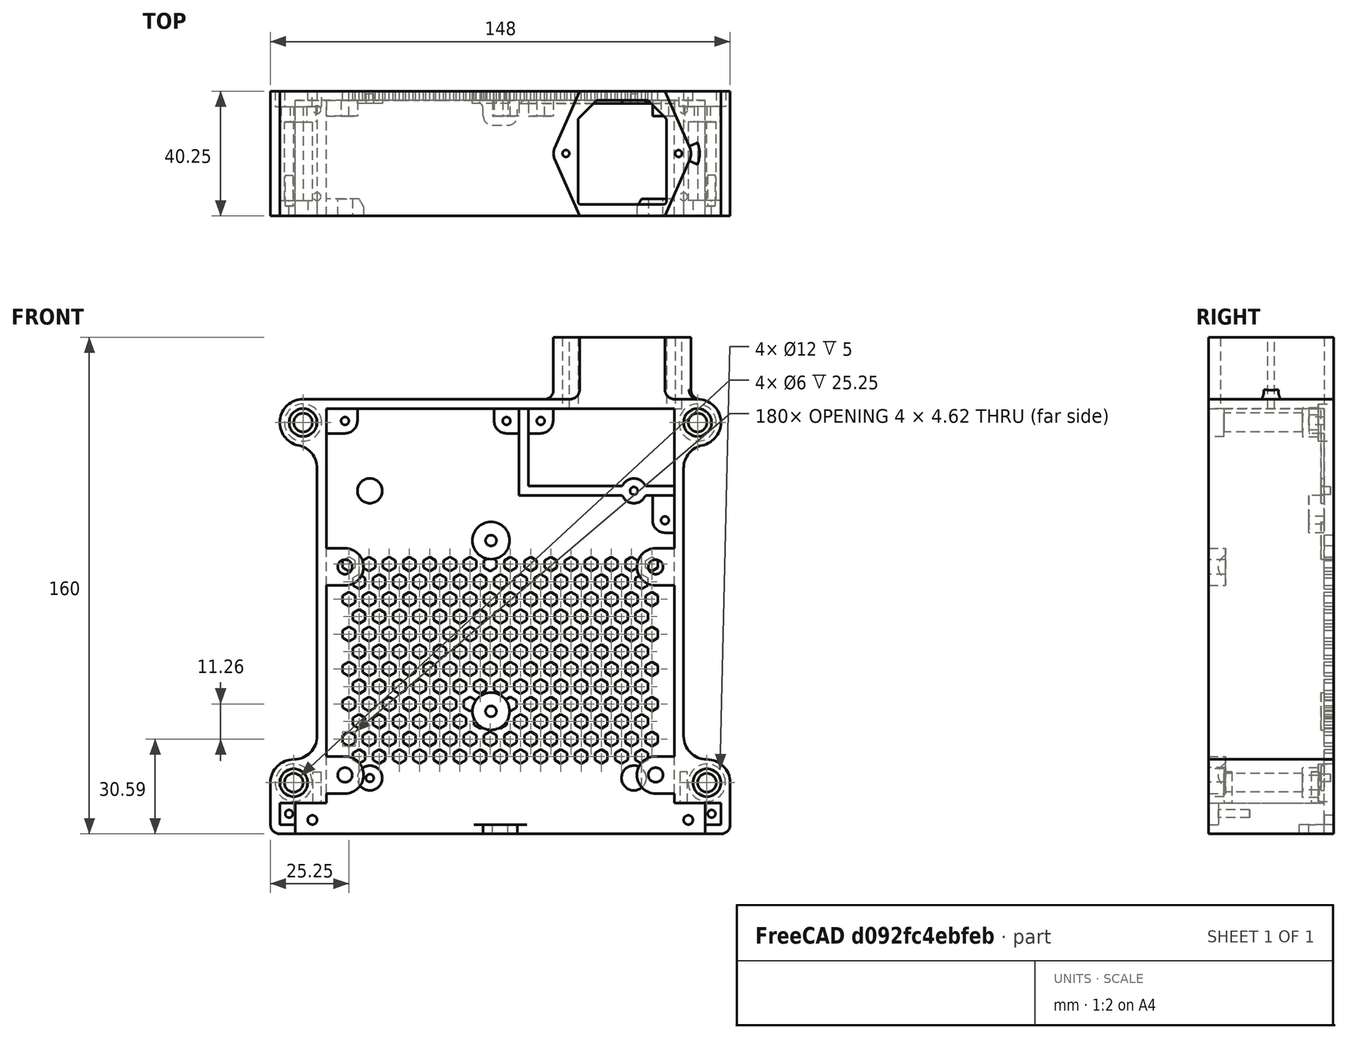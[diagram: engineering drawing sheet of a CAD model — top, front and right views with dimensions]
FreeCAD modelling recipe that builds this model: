
FCSTD DOCUMENT  (FreeCAD 1.0R39319 (Git))
Label: Stack_Module_PSU
License: All rights reserved
LicenseURL: https://en.wikipedia.org/wiki/All_rights_reserved
objects: Sketcher::SketchObject×24, PartDesign::Pocket×17, PartDesign::Pad×7, PartDesign::Fillet×6, PartDesign::LinearPattern×3, PartDesign::MultiTransform×1, PartDesign::Mirrored×1, PartDesign::CoordinateSystem×1, PartDesign::Body×1, App::Part×1
note: 150 computed .brp shape members not serialized (recipe doc carries the construction recipe); baked Part::Feature solids carry a one-line shape summary decoded from their .brp

FEATURE [Sketcher::SketchObject] Sketch
  ArcFitTolerance = 1e-06
  AttachmentSupport = -> [XZ_Plane001]
  FullyConstrained = true
  MakeInternals = false
  MapMode = 5
  Placement = pos=(0,0,0) rot=(1,0,0;1.5708rad)
  sketch-geometry (9):
    g0: LineSegment StartX=0 StartY=-70 StartZ=0 EndX=74 EndY=-70 EndZ=0
    g1: LineSegment StartX=74 StartY=-70 StartZ=0 EndX=74 EndY=-53.5 EndZ=0
    g2: ArcOfCircle CenterX=66.5 CenterY=-53.5 CenterZ=0 NormalX=0 NormalY=0 NormalZ=1 AngleXU=0 Radius=7.5 StartAngle=0 EndAngle=1.5708
    g3: ArcOfCircle CenterX=66.5 CenterY=-38.5 CenterZ=0 NormalX=0 NormalY=0 NormalZ=1 AngleXU=0 Radius=7.5 StartAngle=3.14159 EndAngle=4.71239
    g4: LineSegment StartX=59 StartY=-38.5 StartZ=0 EndX=59 EndY=47.8031 EndZ=0
    g5: ArcOfCircle CenterX=66.5 CenterY=47.8031 CenterZ=0 NormalX=0 NormalY=0 NormalZ=1 AngleXU=0 Radius=7.5 StartAngle=1.77215 EndAngle=3.14159
    g6: ArcOfCircle CenterX=63.5 CenterY=62.5 CenterZ=0 NormalX=0 NormalY=0 NormalZ=1 AngleXU=0 Radius=7.5 StartAngle=4.91375 EndAngle=7.85398
    g7: LineSegment StartX=63.5 StartY=70 StartZ=0 EndX=0 EndY=70 EndZ=0
    g8: LineSegment StartX=0 StartY=70 StartZ=0 EndX=0 EndY=-70 EndZ=0
  constraints (26):
    c: PointOnObject(g0,g-2)
    c: Horizontal(g0)
    c: Coincident(g0,g1)
    c: Vertical(g1)
    c: Tangent(g1,g2) = -1.5708
    c: Tangent(g2,g3) = 1.5708
    c: Tangent(g3,g4) = 1.5708
    c: Tangent(g4,g5) = 1.5708
    c: Tangent(g5,g6) = 1.5708
    c: Tangent(g6,g7) = -1.5708
    c: Coincident(g7,g8)
    c: Coincident(g8,g0)
    c: Vertical(g8)
    c: Horizontal(g7)
    c: Vertical(g4)
    c: DistanceX(g0,g0) = 74
    c: Distance(g7,g0) = 140
    c: Distance(g2,g0) = 16.5
    c: Radius(g2) = 7.5
    c: Distance(g8,g4) = 59
    c: Radius(g6) = 7.5
    c: Distance(g6,g8) = 63.5
    c: Distance(g2,g8) = 66.5
    c: Distance(g-1,g0) = 70
    c: Radius(g3) = 7.5
    c: Radius(g5) = 7.5
FEATURE [PartDesign::Pad] Pad
  Direction = (0,-1,2e-16)
  Length = 40.25
  Length2 = 10
  Placement = pos=(0,0,0) rot=(1,0,0;1.5708rad)
  Profile = -> Sketch
  ReferenceAxis = -> Sketch [N_Axis]
  Refine = true
  Suppressed = false
  Type = 0
FEATURE [Sketcher::SketchObject] Sketch001
  ArcFitTolerance = 1e-06
  AttachmentSupport = -> [Pad]
  ExternalGeometry = -> [Pad]
  FullyConstrained = true
  MakeInternals = false
  MapMode = 5
  Placement = pos=(0,-40.25,0) rot=(1,0,0;1.5708rad)
  sketch-geometry (4):
    g0: LineSegment StartX=0 StartY=-70 StartZ=0 EndX=66 EndY=-70 EndZ=0
    g1: LineSegment StartX=66 StartY=-70 StartZ=0 EndX=66 EndY=-60 EndZ=0
    g2: LineSegment StartX=66 StartY=-60 StartZ=0 EndX=0 EndY=-60 EndZ=0
    g3: LineSegment StartX=0 StartY=-60 StartZ=0 EndX=0 EndY=-70 EndZ=0
  constraints (11):
    c: Coincident(g0,g1)
    c: Coincident(g1,g2)
    c: Coincident(g2,g3)
    c: Coincident(g3,g0)
    c: Horizontal(g0)
    c: Horizontal(g2)
    c: Vertical(g1)
    c: Vertical(g3)
    c: Coincident(g0,g-3)
    c: Distance(g0,g2) = 10
    c: Distance(g1,g3) = 66
FEATURE [PartDesign::Pocket] Pocket
  BaseFeature = -> Pad
  Direction = (0,1,-2e-16)
  Length = 0
  Length2 = 5
  Offset = -3
  Placement = pos=(0,0,0) rot=(1,0,0;1.5708rad)
  Profile = -> Sketch001
  ReferenceAxis = -> Sketch001 [N_Axis]
  Refine = true
  Suppressed = false
  Type = 3
  UpToFace = -> Pad [Face10]
FEATURE [Sketcher::SketchObject] Sketch002
  ArcFitTolerance = 1e-06
  AttachmentSupport = -> [Pocket]
  ExternalGeometry = -> [Pocket]
  FullyConstrained = true
  MakeInternals = false
  MapMode = 5
  Placement = pos=(0,-40.25,0) rot=(1,0,0;1.5708rad)
  sketch-geometry (4):
    g0: LineSegment StartX=0 StartY=67 StartZ=0 EndX=0 EndY=-60 EndZ=0
    g1: LineSegment StartX=0 StartY=-60 StartZ=0 EndX=56 EndY=-60 EndZ=0
    g2: LineSegment StartX=56 StartY=-60 StartZ=0 EndX=56 EndY=67 EndZ=0
    g3: LineSegment StartX=56 StartY=67 StartZ=0 EndX=0 EndY=67 EndZ=0
  constraints (12):
    c: Coincident(g0,g1)
    c: Coincident(g1,g2)
    c: Coincident(g2,g3)
    c: Coincident(g3,g0)
    c: Vertical(g0)
    c: Vertical(g2)
    c: Horizontal(g1)
    c: Horizontal(g3)
    c: PointOnObject(g0,g-2)
    c: PointOnObject(g1,g-5)
    c: Distance(g-4,g2) = 3
    c: Distance(g-3,g3) = 3
FEATURE [PartDesign::Pocket] Pocket001
  BaseFeature = -> Pocket
  Direction = (0,1,-2e-16)
  Length = 0
  Length2 = 5
  Placement = pos=(0,0,0) rot=(1,0,0;1.5708rad)
  Profile = -> Sketch002
  ReferenceAxis = -> Sketch002 [N_Axis]
  Refine = true
  Suppressed = false
  Type = 3
  UpToFace = -> Pocket [Face6]
FEATURE [Sketcher::SketchObject] Sketch003
  ArcFitTolerance = 1e-06
  AttachmentSupport = -> [Pocket001]
  FullyConstrained = true
  MakeInternals = false
  MapMode = 5
  Placement = pos=(0,-3,0) rot=(1,0,0;1.5708rad)
  sketch-geometry (28):
    g0: LineSegment StartX=2 StartY=1.1547 StartZ=0 EndX=0 EndY=2.3094 EndZ=0
    g1: LineSegment StartX=0 StartY=2.3094 StartZ=0 EndX=-2 EndY=1.1547 EndZ=0
    g2: LineSegment StartX=-2 StartY=1.1547 StartZ=0 EndX=-2 EndY=-1.1547 EndZ=0
    g3: LineSegment StartX=-2 StartY=-1.1547 StartZ=0 EndX=0 EndY=-2.3094 EndZ=0
    g4: LineSegment StartX=0 StartY=-2.3094 StartZ=0 EndX=2 EndY=-1.1547 EndZ=0
    g5: LineSegment StartX=2 StartY=-1.1547 StartZ=0 EndX=2 EndY=1.1547 EndZ=0
    g6: Circle [constr] CenterX=0 CenterY=0 CenterZ=0 NormalX=0 NormalY=0 NormalZ=1 AngleXU=0 Radius=2.3094
    g7: LineSegment StartX=5.25 StartY=6.7847 StartZ=0 EndX=3.25 EndY=7.9394 EndZ=0
    g8: LineSegment StartX=3.25 StartY=7.9394 StartZ=0 EndX=1.25 EndY=6.7847 EndZ=0
    g9: LineSegment StartX=1.25 StartY=6.7847 StartZ=0 EndX=1.25 EndY=4.4753 EndZ=0
    g10: LineSegment StartX=1.25 StartY=4.4753 StartZ=0 EndX=3.25 EndY=3.3206 EndZ=0
    g11: LineSegment StartX=3.25 StartY=3.3206 StartZ=0 EndX=5.25 EndY=4.4753 EndZ=0
    g12: LineSegment StartX=5.25 StartY=4.4753 StartZ=0 EndX=5.25 EndY=6.7847 EndZ=0
    g13: Circle [constr] CenterX=3.25 CenterY=5.63 CenterZ=0 NormalX=0 NormalY=0 NormalZ=1 AngleXU=0 Radius=2.3094
    g14: LineSegment StartX=6.5 StartY=2.3094 StartZ=0 EndX=4.5 EndY=1.1547 EndZ=0
    g15: LineSegment StartX=4.5 StartY=1.1547 StartZ=0 EndX=4.5 EndY=-1.1547 EndZ=0
    g16: LineSegment StartX=4.5 StartY=-1.1547 StartZ=0 EndX=6.5 EndY=-2.3094 EndZ=0
    g17: LineSegment StartX=6.5 StartY=-2.3094 StartZ=0 EndX=8.5 EndY=-1.1547 EndZ=0
    g18: LineSegment StartX=8.5 StartY=-1.1547 StartZ=0 EndX=8.5 EndY=1.1547 EndZ=0
    g19: LineSegment StartX=8.5 StartY=1.1547 StartZ=0 EndX=6.5 EndY=2.3094 EndZ=0
    g20: Circle [constr] CenterX=6.5 CenterY=0 CenterZ=0 NormalX=0 NormalY=0 NormalZ=1 AngleXU=0 Radius=2.3094
    g21: LineSegment StartX=11.75 StartY=6.7847 StartZ=0 EndX=9.75 EndY=7.9394 EndZ=0
    g22: LineSegment StartX=9.75 StartY=7.9394 StartZ=0 EndX=7.75 EndY=6.7847 EndZ=0
    g23: LineSegment StartX=7.75 StartY=6.7847 StartZ=0 EndX=7.75 EndY=4.4753 EndZ=0
    g24: LineSegment StartX=7.75 StartY=4.4753 StartZ=0 EndX=9.75 EndY=3.3206 EndZ=0
    g25: LineSegment StartX=9.75 StartY=3.3206 StartZ=0 EndX=11.75 EndY=4.4753 EndZ=0
    g26: LineSegment StartX=11.75 StartY=4.4753 StartZ=0 EndX=11.75 EndY=6.7847 EndZ=0
    g27: Circle [constr] CenterX=9.75 CenterY=5.63 CenterZ=0 NormalX=0 NormalY=0 NormalZ=1 AngleXU=0 Radius=2.3094
  constraints (70):
    c: Coincident(g0,g1)
    c: Coincident(g1,g2)
    c: Coincident(g2,g3)
    c: Coincident(g3,g4)
    c: Coincident(g4,g5)
    c: Coincident(g5,g0)
    c: Equal(g0, g1-g5) x5
    c: PointOnObject(g0,g6)
    c: PointOnObject(g1,g6)
    c: PointOnObject(g2,g6)
    c: PointOnObject(g3,g6)
    c: PointOnObject(g4,g6)
    c: PointOnObject(g5,g6)
    c: Coincident(g6,g-1)
    c: PointOnObject(g0,g-2)
    c: Distance(g5,g2) = 4
    c: Coincident(g7,g8)
    c: Coincident(g8,g9)
    c: Coincident(g9,g10)
    c: Coincident(g10,g11)
    c: Coincident(g11,g12)
    c: Coincident(g12,g7)
    c: Equal(g7, g8-g12) x5
    c: PointOnObject(g7,g13)
    c: PointOnObject(g8,g13)
    c: PointOnObject(g9,g13)
    c: PointOnObject(g10,g13)
    c: PointOnObject(g11,g13)
    c: PointOnObject(g12,g13)
    c: Distance(g13,g-2) = 3.25
    c: DistanceY(g6,g13) = 5.63
    c: Vertical(g9)
    c: Coincident(g14,g15)
    c: Coincident(g15,g16)
    c: Coincident(g16,g17)
    c: Coincident(g17,g18)
    c: Coincident(g18,g19)
    c: Coincident(g19,g14)
    c: Equal(g14, g15-g19) x5
    c: PointOnObject(g14,g20)
    c: PointOnObject(g15,g20)
    c: PointOnObject(g16,g20)
    c: PointOnObject(g17,g20)
    c: PointOnObject(g18,g20)
    c: PointOnObject(g19,g20)
    c: PointOnObject(g20,g-1)
    c: Distance(g20,g-2) = 6.5
    c: Vertical(g15)
    c: Distance(g15,g5) = 2.5
    c: Distance(g10,g0) = 2.50072
    c: Distance(g5,g2) = 4
    c: Distance(g18,g15) = 4
    c: Distance(g12,g9) = 4
    c: Coincident(g21,g22)
    c: Coincident(g22,g23)
    c: Coincident(g23,g24)
    c: Coincident(g24,g25)
    c: Coincident(g25,g26)
    c: Coincident(g26,g21)
    c: Equal(g21, g22-g26) x5
    c: PointOnObject(g21,g27)
    c: PointOnObject(g22,g27)
    c: PointOnObject(g23,g27)
    c: PointOnObject(g24,g27)
    c: PointOnObject(g25,g27)
    c: PointOnObject(g26,g27)
    c: Vertical(g23)
    c: Distance(g26,g23) = 4
    c: Distance(g27,g-1) = 5.63
    c: DistanceX(g13,g27) = 6.5
FEATURE [PartDesign::Pocket] Pocket002
  BaseFeature = -> Pocket001
  Direction = (0,1,-2e-16)
  Length = 5
  Length2 = 5
  Placement = pos=(0,0,0) rot=(1,0,0;1.5708rad)
  Profile = -> Sketch003
  ReferenceAxis = -> Sketch003 [N_Axis]
  Refine = true
  Suppressed = false
  Type = 1
FEATURE [PartDesign::LinearPattern] LinearPattern
  Direction = -> X_Axis001
  Length = 39
  Mode = 1
  Occurrences = 4
  Offset = 13
  Placement = pos=(0,0,0) rot=(1,0,0;1.5708rad)
  Refine = true
  Suppressed = false
  TransformMode = 0
FEATURE [PartDesign::LinearPattern] LinearPattern001
  Direction = -> Z_Axis001
  Length = 45.04
  Mode = 1
  Occurrences = 5
  Offset = 11.26
  Placement = pos=(0,0,0) rot=(1,0,0;1.5708rad)
  Refine = true
  Reversed = true
  Suppressed = false
  TransformMode = 0
FEATURE [PartDesign::LinearPattern] LinearPattern002
  Direction = -> Z_Axis001
  Length = 11.26
  Mode = 1
  Occurrences = 2
  Offset = 11.26
  Placement = pos=(0,0,0) rot=(1,0,0;1.5708rad)
  Refine = true
  Suppressed = false
  TransformMode = 0
FEATURE [PartDesign::MultiTransform] MultiTransform
  BaseFeature = -> Pocket002
  Originals = -> [Pocket002]
  Placement = pos=(0,0,0) rot=(1,0,0;1.5708rad)
  Refine = true
  Suppressed = false
  TransformMode = 0
  Transformations = -> [LinearPattern,LinearPattern001,LinearPattern002]
FEATURE [Sketcher::SketchObject] Sketch004
  ArcFitTolerance = 1e-06
  AttachmentSupport = -> [MultiTransform]
  ExternalGeometry = -> [MultiTransform]
  FullyConstrained = true
  MakeInternals = false
  MapMode = 5
  Placement = pos=(0,-40.25,0) rot=(1,0,0;1.5708rad)
  sketch-geometry (11):
    g0: LineSegment StartX=56 StartY=-45 StartZ=0 EndX=50 EndY=-45 EndZ=0
    g1: ArcOfCircle CenterX=50 CenterY=-51 CenterZ=0 NormalX=0 NormalY=0 NormalZ=1 AngleXU=0 Radius=6 StartAngle=1.5708 EndAngle=4.71239
    g2: LineSegment StartX=50 StartY=-57 StartZ=0 EndX=56 EndY=-57 EndZ=0
    g3: LineSegment StartX=56 StartY=-57 StartZ=0 EndX=56 EndY=-45 EndZ=0
    g4: LineSegment StartX=56 StartY=22 StartZ=0 EndX=50 EndY=22 EndZ=0
    g5: ArcOfCircle CenterX=50 CenterY=16 CenterZ=0 NormalX=0 NormalY=0 NormalZ=1 AngleXU=0 Radius=6 StartAngle=1.5708 EndAngle=4.71239
    g6: LineSegment StartX=50 StartY=10 StartZ=0 EndX=56 EndY=10 EndZ=0
    g7: LineSegment StartX=56 StartY=10 StartZ=0 EndX=56 EndY=22 EndZ=0
    g8: LineSegment [constr] StartX=50 StartY=16 StartZ=0 EndX=50 EndY=-51 EndZ=0
    g9: Circle CenterX=50 CenterY=16 CenterZ=0 NormalX=0 NormalY=0 NormalZ=1 AngleXU=0 Radius=2.35
    g10: Circle CenterX=50 CenterY=-51 CenterZ=0 NormalX=0 NormalY=0 NormalZ=1 AngleXU=0 Radius=2.35
  constraints (28):
    c: Horizontal(g0)
    c: Tangent(g0,g1) = -1.5708
    c: Tangent(g1,g2) = -1.5708
    c: Coincident(g2,g3)
    c: Coincident(g3,g0)
    c: Vertical(g3)
    c: Horizontal(g2)
    c: Horizontal(g4)
    c: Tangent(g4,g5) = -1.5708
    c: Tangent(g5,g6) = -1.5708
    c: Coincident(g6,g7)
    c: Coincident(g7,g4)
    c: Vertical(g7)
    c: Horizontal(g6)
    c: Coincident(g8,g5)
    c: Coincident(g8,g1)
    c: Vertical(g8)
    c: PointOnObject(g4,g-3)
    c: PointOnObject(g0,g-3)
    c: Distance(g6,g4) = 12
    c: Distance(g2,g0) = 12
    c: Distance(g2,g-4) = 13
    c: DistanceY(g8,g8) = 67
    c: Distance(g-2,g8) = 50
    c: Coincident(g9,g5)
    c: Coincident(g10,g1)
    c: Diameter(g10) = 4.7
    c: Diameter(g9) = 4.7
FEATURE [PartDesign::Pad] Pad001
  BaseFeature = -> MultiTransform
  Direction = (0,-1,2e-16)
  Length = 5.5
  Length2 = 10
  Placement = pos=(0,0,0) rot=(1,0,0;1.5708rad)
  Profile = -> Sketch004
  ReferenceAxis = -> Sketch004 [N_Axis]
  Refine = true
  Reversed = true
  Suppressed = false
  Type = 0
FEATURE [Sketcher::SketchObject] Sketch006
  ArcFitTolerance = 1e-06
  AttachmentSupport = -> [Pad001]
  ExternalGeometry = -> [Pad001]
  FullyConstrained = true
  MakeInternals = false
  MapMode = 5
  Placement = pos=(0,-3.08e-14,-70) rot=(1,0,0;3.14159rad)
  sketch-geometry (3):
    g0: LineSegment StartX=44 StartY=37.25 StartZ=0 EndX=44 EndY=34.75 EndZ=0
    g1: LineSegment StartX=44 StartY=34.75 StartZ=0 EndX=45.4434 EndY=34.75 EndZ=0
    g2: LineSegment StartX=45.4434 StartY=34.75 StartZ=0 EndX=44 EndY=37.25 EndZ=0
  constraints (9):
    c: Vertical(g0)
    c: Coincident(g0,g1)
    c: Horizontal(g1)
    c: Coincident(g1,g2)
    c: Coincident(g2,g0)
    c: Distance(g0,g-4) = 3
    c: Distance(g-3,g0) = 12
    c: PointOnObject(g1,g-5)
    c: Angle(g0,g2) = 0.523599
FEATURE [PartDesign::Pocket] Pocket003
  BaseFeature = -> Pad001
  Direction = (0,0,1)
  Length = 0
  Length2 = 5
  Placement = pos=(0,0,0) rot=(1,0,0;1.5708rad)
  Profile = -> Sketch006
  ReferenceAxis = -> Sketch006 [N_Axis]
  Refine = true
  Suppressed = false
  Type = 3
  UpToFace = -> Pad001 [Face585]
FEATURE [Sketcher::SketchObject] Sketch007
  ArcFitTolerance = 1e-06
  AttachmentSupport = -> [Pocket003]
  ExternalGeometry = -> [Pocket003]
  FullyConstrained = true
  MakeInternals = false
  MapMode = 5
  Placement = pos=(0,-40.25,1.69e-14) rot=(1,0,0;1.5708rad)
  sketch-geometry (4):
    g0: LineSegment StartX=66 StartY=-60 StartZ=0 EndX=66 EndY=-67 EndZ=0
    g1: LineSegment StartX=66 StartY=-67 StartZ=0 EndX=71 EndY=-67 EndZ=0
    g2: LineSegment StartX=71 StartY=-67 StartZ=0 EndX=71 EndY=-60 EndZ=0
    g3: LineSegment StartX=71 StartY=-60 StartZ=0 EndX=66 EndY=-60 EndZ=0
  constraints (11):
    c: Coincident(g0,g1)
    c: Coincident(g1,g2)
    c: Coincident(g2,g3)
    c: Coincident(g3,g0)
    c: Vertical(g0)
    c: Vertical(g2)
    c: Horizontal(g1)
    c: Horizontal(g3)
    c: Coincident(g0,g-3)
    c: Distance(g1,g3) = 7
    c: Distance(g2,g0) = 5
FEATURE [PartDesign::Pocket] Pocket004
  BaseFeature = -> Pocket003
  Direction = (0,1,-2e-16)
  Length = 3.2
  Length2 = 5
  Placement = pos=(0,0,0) rot=(1,0,0;1.5708rad)
  Profile = -> Sketch007
  ReferenceAxis = -> Sketch007 [N_Axis]
  Refine = true
  Suppressed = false
  Type = 0
FEATURE [Sketcher::SketchObject] Sketch008
  ArcFitTolerance = 1e-06
  AttachmentSupport = -> [Pocket004]
  ExternalGeometry = -> [Pocket004]
  FullyConstrained = true
  MakeInternals = false
  MapMode = 5
  Placement = pos=(0,-37.05,0) rot=(1,0,0;1.5708rad)
  sketch-geometry (1):
    g0: Circle CenterX=68 CenterY=-63.5 CenterZ=0 NormalX=0 NormalY=0 NormalZ=1 AngleXU=0 Radius=1.25
  constraints (3):
    c: Diameter(g0) = 2.5
    c: Distance(g0,g-2) = 68
    c: Distance(g0,g-3) = 3.5
FEATURE [PartDesign::Pocket] Pocket005
  BaseFeature = -> Pocket004
  Direction = (0,1,-2e-16)
  Length = 10
  Length2 = 5
  Placement = pos=(0,0,0) rot=(1,0,0;1.5708rad)
  Profile = -> Sketch008
  ReferenceAxis = -> Sketch008 [N_Axis]
  Refine = true
  Suppressed = false
  Type = 0
FEATURE [Sketcher::SketchObject] Sketch009
  ArcFitTolerance = 1e-06
  AttachmentSupport = -> [Pocket005]
  ExternalGeometry = -> [Pocket005]
  FullyConstrained = true
  MakeInternals = false
  MapMode = 5
  Placement = pos=(0,-3,0) rot=(1,0,0;1.5708rad)
  sketch-geometry (1):
    g0: Circle CenterX=60.5 CenterY=-65.5 CenterZ=0 NormalX=0 NormalY=0 NormalZ=1 AngleXU=0 Radius=1.5
  constraints (3):
    c: Diameter(g0) = 3
    c: Distance(g0,g-3) = 4.5
    c: Distance(g0,g-2) = 60.5
FEATURE [PartDesign::Pocket] Pocket006
  BaseFeature = -> Pocket005
  Direction = (0,1,-2e-16)
  Length = 5
  Length2 = 5
  Placement = pos=(0,0,0) rot=(1,0,0;1.5708rad)
  Profile = -> Sketch009
  ReferenceAxis = -> Sketch009 [N_Axis]
  Refine = true
  Suppressed = false
  Type = 1
FEATURE [Sketcher::SketchObject] Sketch010
  ArcFitTolerance = 1e-06
  AttachmentSupport = -> [Pocket006]
  ExternalGeometry = -> [Pocket006]
  FullyConstrained = true
  MakeInternals = false
  MapMode = 5
  Placement = pos=(3.24e-14,-2.28e-14,-60) rot=(1,0,0;3.14159rad)
  sketch-geometry (3):
    g0: LineSegment [constr] StartX=59 StartY=34 StartZ=0 EndX=59 EndY=6 EndZ=0
    g1: Circle CenterX=59 CenterY=34 CenterZ=0 NormalX=0 NormalY=0 NormalZ=1 AngleXU=0 Radius=1.25
    g2: Circle CenterX=59 CenterY=6 CenterZ=0 NormalX=0 NormalY=0 NormalZ=1 AngleXU=0 Radius=1.25
  constraints (8):
    c: Vertical(g0)
    c: Coincident(g1,g0)
    c: Coincident(g2,g0)
    c: Distance(g0,g-3) = 31
    c: Distance(g-4,g0) = 3
    c: Distance(g0,g-3) = 3
    c: Diameter(g2) = 2.5
    c: Diameter(g1) = 2.5
FEATURE [PartDesign::Pocket] Pocket007
  BaseFeature = -> Pocket006
  Direction = (0,0,1)
  Length = 10
  Length2 = 5
  Placement = pos=(0,0,0) rot=(1,0,0;1.5708rad)
  Profile = -> Sketch010
  ReferenceAxis = -> Sketch010 [N_Axis]
  Refine = true
  Suppressed = false
  Type = 0
FEATURE [Sketcher::SketchObject] Sketch011
  ArcFitTolerance = 1e-06
  AttachmentSupport = -> [Pocket007]
  ExternalGeometry = -> [Pocket007]
  FullyConstrained = true
  MakeInternals = false
  MapMode = 5
  Placement = pos=(0,-40.25,1.69e-14) rot=(1,0,0;1.5708rad)
  sketch-geometry (2):
    g0: Circle CenterX=63.5 CenterY=62.5 CenterZ=0 NormalX=0 NormalY=0 NormalZ=1 AngleXU=0 Radius=3
    g1: Circle CenterX=66.5 CenterY=-53.5 CenterZ=0 NormalX=0 NormalY=0 NormalZ=1 AngleXU=0 Radius=3
  constraints (7):
    c: Coincident(g0,g-3)
    c: Coincident(g1,g-4)
    c: Diameter(g0) = 6
    c: Diameter(g1) = 6
    c: DistanceY(g1,g0) = 116
    c: Distance(g0,g-2) = 63.5
    c: DistanceX(g-1,g1) = 66.5
FEATURE [PartDesign::Pocket] Pocket008
  BaseFeature = -> Pocket007
  Direction = (0,1,-2e-16)
  Length = 5
  Length2 = 5
  Placement = pos=(0,0,0) rot=(1,0,0;1.5708rad)
  Profile = -> Sketch011
  ReferenceAxis = -> Sketch011 [N_Axis]
  Refine = true
  Suppressed = false
  Type = 1
FEATURE [Sketcher::SketchObject] Sketch012
  ArcFitTolerance = 1e-06
  AttachmentSupport = -> [Pocket008]
  ExternalGeometry = -> [Pocket008]
  FullyConstrained = true
  MakeInternals = false
  MapMode = 5
  Placement = pos=(0,-40.25,1.69e-14) rot=(1,0,0;1.5708rad)
  sketch-geometry (2):
    g0: Circle CenterX=63.5 CenterY=62.5 CenterZ=0 NormalX=0 NormalY=0 NormalZ=1 AngleXU=0 Radius=4.5
    g1: Circle CenterX=66.5 CenterY=-53.5 CenterZ=0 NormalX=0 NormalY=0 NormalZ=1 AngleXU=0 Radius=4.5
  constraints (4):
    c: Coincident(g0,g-4)
    c: Coincident(g1,g-3)
    c: Diameter(g1) = 9
    c: Diameter(g0) = 9
FEATURE [PartDesign::Pocket] Pocket009
  BaseFeature = -> Pocket008
  Direction = (0,1,-2e-16)
  Length = 5
  Length2 = 5
  Placement = pos=(0,0,0) rot=(1,0,0;1.5708rad)
  Profile = -> Sketch012
  ReferenceAxis = -> Sketch012 [N_Axis]
  Refine = true
  Suppressed = false
  Type = 0
FEATURE [Sketcher::SketchObject] Sketch013
  ArcFitTolerance = 1e-06
  AttachmentSupport = -> [Pocket009]
  ExternalGeometry = -> [Pocket009]
  FullyConstrained = true
  MakeInternals = false
  MapMode = 5
  Placement = pos=(0,-3e-16,0) rot=(-1,0,0;1.5708rad)
  sketch-geometry (2):
    g0: Circle CenterX=63.5 CenterY=-62.5 CenterZ=0 NormalX=0 NormalY=0 NormalZ=1 AngleXU=0 Radius=6
    g1: Circle CenterX=66.5 CenterY=53.5 CenterZ=0 NormalX=0 NormalY=0 NormalZ=1 AngleXU=0 Radius=6
  constraints (4):
    c: Coincident(g0,g-4)
    c: Coincident(g1,g-3)
    c: Diameter(g1) = 12
    c: Diameter(g0) = 12
FEATURE [PartDesign::Pocket] Pocket010
  BaseFeature = -> Pocket009
  Direction = (0,-1,-2e-16)
  Length = 5
  Length2 = 5
  Placement = pos=(0,0,0) rot=(1,0,0;1.5708rad)
  Profile = -> Sketch013
  ReferenceAxis = -> Sketch013 [N_Axis]
  Refine = true
  Suppressed = false
  Type = 0
FEATURE [Sketcher::SketchObject] Sketch014
  ArcFitTolerance = 1e-06
  AttachmentSupport = -> [Pocket010]
  ExternalGeometry = -> [Pocket010]
  FullyConstrained = true
  MakeInternals = false
  MapMode = 5
  Placement = pos=(0,-5,0) rot=(-1,0,0;1.5708rad)
  sketch-geometry (14):
    g0: LineSegment StartX=66.5 StartY=58.25 StartZ=0 EndX=62.3864 EndY=55.875 EndZ=0
    g1: LineSegment StartX=62.3864 StartY=55.875 StartZ=0 EndX=62.3864 EndY=51.125 EndZ=0
    g2: LineSegment StartX=62.3864 StartY=51.125 StartZ=0 EndX=66.5 EndY=48.75 EndZ=0
    g3: LineSegment StartX=66.5 StartY=48.75 StartZ=0 EndX=70.6136 EndY=51.125 EndZ=0
    g4: LineSegment StartX=70.6136 StartY=51.125 StartZ=0 EndX=70.6136 EndY=55.875 EndZ=0
    g5: LineSegment StartX=70.6136 StartY=55.875 StartZ=0 EndX=66.5 EndY=58.25 EndZ=0
    g6: Circle [constr] CenterX=66.5 CenterY=53.5 CenterZ=0 NormalX=0 NormalY=0 NormalZ=1 AngleXU=0 Radius=4.75
    g7: LineSegment StartX=67.6136 StartY=-60.125 StartZ=0 EndX=63.5 EndY=-57.75 EndZ=0
    g8: LineSegment StartX=63.5 StartY=-57.75 StartZ=0 EndX=59.3864 EndY=-60.125 EndZ=0
    g9: LineSegment StartX=59.3864 StartY=-60.125 StartZ=0 EndX=59.3864 EndY=-64.875 EndZ=0
    g10: LineSegment StartX=59.3864 StartY=-64.875 StartZ=0 EndX=63.5 EndY=-67.25 EndZ=0
    g11: LineSegment StartX=63.5 StartY=-67.25 StartZ=0 EndX=67.6136 EndY=-64.875 EndZ=0
    g12: LineSegment StartX=67.6136 StartY=-64.875 StartZ=0 EndX=67.6136 EndY=-60.125 EndZ=0
    g13: Circle [constr] CenterX=63.5 CenterY=-62.5 CenterZ=0 NormalX=0 NormalY=0 NormalZ=1 AngleXU=0 Radius=4.75
  constraints (32):
    c: Coincident(g0,g1)
    c: Coincident(g1,g2)
    c: Coincident(g2,g3)
    c: Coincident(g3,g4)
    c: Coincident(g4,g5)
    c: Coincident(g5,g0)
    c: Equal(g0, g1-g5) x5
    c: PointOnObject(g0,g6)
    c: PointOnObject(g1,g6)
    c: PointOnObject(g2,g6)
    c: PointOnObject(g3,g6)
    c: PointOnObject(g4,g6)
    c: PointOnObject(g5,g6)
    c: Coincident(g7,g8)
    c: Coincident(g8,g9)
    c: Coincident(g9,g10)
    c: Coincident(g10,g11)
    c: Coincident(g11,g12)
    c: Coincident(g12,g7)
    c: Equal(g7, g8-g12) x5
    c: PointOnObject(g7,g13)
    c: PointOnObject(g8,g13)
    c: PointOnObject(g9,g13)
    c: PointOnObject(g10,g13)
    c: PointOnObject(g11,g13)
    c: PointOnObject(g12,g13)
    c: Coincident(g13,g-4)
    c: Diameter(g13) = 9.5
    c: Diameter(g6) = 9.5
    c: Coincident(g-3,g6)
    c: Vertical(g1)
    c: Vertical(g9)
FEATURE [PartDesign::Pocket] Pocket011
  BaseFeature = -> Pocket010
  Direction = (0,-1,-2e-16)
  Length = 5
  Length2 = 5
  Placement = pos=(0,0,0) rot=(1,0,0;1.5708rad)
  Profile = -> Sketch014
  ReferenceAxis = -> Sketch014 [N_Axis]
  Refine = true
  Suppressed = false
  Type = 0
FEATURE [PartDesign::Fillet] Fillet
  Base = -> Pocket011 [Edge2]
  BaseFeature = -> Pocket011
  Placement = pos=(0,0,0) rot=(1,0,0;1.5708rad)
  Radius = 3
  Refine = true
  SupportTransform = false
  Suppressed = false
  UseAllEdges = false
FEATURE [Sketcher::SketchObject] Sketch015
  ArcFitTolerance = 1e-06
  AttachmentSupport = -> [Fillet]
  ExternalGeometry = -> [Fillet]
  FullyConstrained = true
  MakeInternals = false
  MapMode = 5
  Placement = pos=(0,-3.08e-14,-70) rot=(1,0,0;3.14159rad)
  sketch-geometry (6):
    g0: LineSegment StartX=2.5 StartY=3 StartZ=0 EndX=2.5 EndY=8 EndZ=0
    g1: LineSegment StartX=2.5 StartY=8 StartZ=0 EndX=0 EndY=8 EndZ=0
    g2: LineSegment StartX=0 StartY=8 StartZ=0 EndX=0 EndY=11 EndZ=0
    g3: LineSegment StartX=0 StartY=11 StartZ=0 EndX=5.5 EndY=11 EndZ=0
    g4: LineSegment StartX=5.5 StartY=11 StartZ=0 EndX=5.5 EndY=3 EndZ=0
    g5: LineSegment StartX=5.5 StartY=3 StartZ=0 EndX=2.5 EndY=3 EndZ=0
  constraints (18):
    c: PointOnObject(g0,g-3)
    c: Vertical(g0)
    c: Coincident(g0,g1)
    c: PointOnObject(g1,g-2)
    c: Horizontal(g1)
    c: Coincident(g1,g2)
    c: PointOnObject(g2,g-2)
    c: Coincident(g2,g3)
    c: Horizontal(g3)
    c: Coincident(g3,g4)
    c: PointOnObject(g4,g-3)
    c: Vertical(g4)
    c: Coincident(g4,g5)
    c: Coincident(g5,g0)
    c: Distance(g1,g3) = 3
    c: Distance(g-2,g0) = 2.5
    c: Distance(g4,g0) = 3
    c: Distance(g1,g-3) = 5
FEATURE [PartDesign::Pad] Pad002
  BaseFeature = -> Fillet
  Direction = (0,0,-1)
  Length = 3
  Length2 = 10
  Placement = pos=(0,0,0) rot=(1,0,0;1.5708rad)
  Profile = -> Sketch015
  ReferenceAxis = -> Sketch015 [N_Axis]
  Refine = true
  Reversed = true
  Suppressed = false
  Type = 0
FEATURE [PartDesign::Fillet] Fillet001
  Base = -> Pad002 [Edge1804,Edge624]
  BaseFeature = -> Pad002
  Placement = pos=(0,0,0) rot=(1,0,0;1.5708rad)
  Radius = 3
  Refine = true
  SupportTransform = false
  Suppressed = false
  UseAllEdges = false
FEATURE [PartDesign::Mirrored] Mirrored
  BaseFeature = -> Fillet001
  MirrorPlane = -> YZ_Plane001
  Placement = pos=(0,0,0) rot=(1,0,0;1.5708rad)
  Refine = true
  Suppressed = false
  TransformMode = 1
FEATURE [Sketcher::SketchObject] Sketch016
  ArcFitTolerance = 1e-06
  AttachmentSupport = -> [Mirrored]
  ExternalGeometry = -> [Mirrored]
  FullyConstrained = true
  MakeInternals = false
  MapMode = 5
  Placement = pos=(0,5.7e-15,0) rot=(-1,0,0;1.5708rad)
  sketch-geometry (11):
    g0: Circle CenterX=-3 CenterY=30.5 CenterZ=0 NormalX=0 NormalY=0 NormalZ=1 AngleXU=0 Radius=6
    g1: Circle CenterX=-3 CenterY=-24.5 CenterZ=0 NormalX=0 NormalY=0 NormalZ=1 AngleXU=0 Radius=6
    g2: LineSegment [constr] StartX=-42 StartY=52 StartZ=0 EndX=-42 EndY=-40.5 EndZ=0
    g3: LineSegment [constr] StartX=-42 StartY=-40.5 StartZ=0 EndX=43 EndY=-40.5 EndZ=0
    g4: LineSegment [constr] StartX=43 StartY=-40.5 StartZ=0 EndX=43 EndY=52 EndZ=0
    g5: LineSegment [constr] StartX=43 StartY=52 StartZ=0 EndX=-42 EndY=52 EndZ=0
    g6: Circle CenterX=-42 CenterY=52 CenterZ=0 NormalX=0 NormalY=0 NormalZ=1 AngleXU=0 Radius=4
    g7: Circle CenterX=43 CenterY=52 CenterZ=0 NormalX=0 NormalY=0 NormalZ=1 AngleXU=0 Radius=4
    g8: Circle CenterX=43 CenterY=-40.5 CenterZ=0 NormalX=0 NormalY=0 NormalZ=1 AngleXU=0 Radius=4
    g9: Circle CenterX=-42 CenterY=-40.5 CenterZ=0 NormalX=0 NormalY=0 NormalZ=1 AngleXU=0 Radius=4
    g10: LineSegment [constr] StartX=-3 StartY=30.5 StartZ=0 EndX=-3 EndY=-24.5 EndZ=0
  constraints (28):
    c: Coincident(g2,g3)
    c: Coincident(g3,g4)
    c: Coincident(g4,g5)
    c: Coincident(g5,g2)
    c: Vertical(g2)
    c: Vertical(g4)
    c: Horizontal(g3)
    c: Horizontal(g5)
    c: Coincident(g6,g2)
    c: Coincident(g7,g4)
    c: Coincident(g8,g3)
    c: Coincident(g9,g2)
    c: Coincident(g10,g0)
    c: Coincident(g10,g1)
    c: Vertical(g10)
    c: Diameter(g6) = 8
    c: Diameter(g7) = 8
    c: Diameter(g9) = 8
    c: Diameter(g8) = 8
    c: Diameter(g0) = 12
    c: Diameter(g1) = 12
    c: Distance(g10,g-2) = 3
    c: Distance(g3,g5) = 92.5
    c: Distance(g4,g2) = 85
    c: Distance(g2,g10) = 39
    c: DistanceY(g1,g0) = 55
    c: Distance(g1,g3) = 16
    c: Distance(g5,g-3) = 8
FEATURE [PartDesign::Pad] Pad003
  BaseFeature = -> Mirrored
  Direction = (0,1,2e-16)
  Length = 10
  Length2 = 10
  Offset = 1
  Placement = pos=(0,0,0) rot=(1,0,0;1.5708rad)
  Profile = -> Sketch016
  ReferenceAxis = -> Sketch016 [N_Axis]
  Refine = true
  Reversed = true
  Suppressed = false
  Type = 3
  UpToFace = -> Mirrored [Face25]
FEATURE [Sketcher::SketchObject] Sketch017
  ArcFitTolerance = 1e-06
  AttachmentSupport = -> [Pad003]
  ExternalGeometry = -> [Pad003]
  FullyConstrained = true
  MakeInternals = false
  MapMode = 5
  Placement = pos=(0,-4,0) rot=(1,0,0;1.5708rad)
  sketch-geometry (2):
    g0: Circle CenterX=-3 CenterY=24.5 CenterZ=0 NormalX=0 NormalY=0 NormalZ=1 AngleXU=0 Radius=1.75
    g1: Circle CenterX=-3 CenterY=-30.5 CenterZ=0 NormalX=0 NormalY=0 NormalZ=1 AngleXU=0 Radius=1.75
  constraints (4):
    c: Coincident(g0,g-3)
    c: Coincident(g1,g-4)
    c: Diameter(g0) = 3.5
    c: Diameter(g1) = 3.5
FEATURE [PartDesign::Pocket] Pocket012
  BaseFeature = -> Pad003
  Direction = (0,1,-2e-16)
  Length = 5
  Length2 = 5
  Placement = pos=(0,0,0) rot=(1,0,0;1.5708rad)
  Profile = -> Sketch017
  ReferenceAxis = -> Sketch017 [N_Axis]
  Refine = true
  Suppressed = false
  Type = 1
FEATURE [Sketcher::SketchObject] Sketch018
  ArcFitTolerance = 1e-06
  AttachmentSupport = -> [Pocket012]
  ExternalGeometry = -> [Pocket012]
  FullyConstrained = true
  MakeInternals = false
  MapMode = 5
  Placement = pos=(0,-4,0) rot=(1,0,0;1.5708rad)
  sketch-geometry (2):
    g0: Circle CenterX=43 CenterY=40.5 CenterZ=0 NormalX=0 NormalY=0 NormalZ=1 AngleXU=0 Radius=1.25
    g1: Circle CenterX=-42 CenterY=-52 CenterZ=0 NormalX=0 NormalY=0 NormalZ=1 AngleXU=0 Radius=1.25
  constraints (4):
    c: Coincident(g0,g-3)
    c: Coincident(g1,g-4)
    c: Diameter(g1) = 2.5
    c: Diameter(g0) = 2.5
FEATURE [Sketcher::SketchObject] Sketch019
  ArcFitTolerance = 1e-06
  AttachmentSupport = -> [Pocket012]
  ExternalGeometry = -> [Pocket012]
  FullyConstrained = true
  MakeInternals = false
  MapMode = 5
  Placement = pos=(0,-3,0) rot=(1,0,0;1.5708rad)
  sketch-geometry (6):
    g0: LineSegment StartX=9 StartY=67 StartZ=0 EndX=9 EndY=42 EndZ=0
    g1: LineSegment StartX=9 StartY=42 StartZ=0 EndX=56 EndY=42 EndZ=0
    g2: LineSegment StartX=56 StartY=42 StartZ=0 EndX=56 EndY=39 EndZ=0
    g3: LineSegment StartX=56 StartY=39 StartZ=0 EndX=6 EndY=39 EndZ=0
    g4: LineSegment StartX=6 StartY=39 StartZ=0 EndX=6 EndY=67 EndZ=0
    g5: LineSegment StartX=6 StartY=67 StartZ=0 EndX=9 EndY=67 EndZ=0
  constraints (18):
    c: PointOnObject(g0,g-3)
    c: Vertical(g0)
    c: Coincident(g0,g1)
    c: PointOnObject(g1,g-4)
    c: Horizontal(g1)
    c: Coincident(g1,g2)
    c: PointOnObject(g2,g-4)
    c: Coincident(g2,g3)
    c: Horizontal(g3)
    c: Coincident(g3,g4)
    c: PointOnObject(g4,g-3)
    c: Vertical(g4)
    c: Coincident(g4,g5)
    c: Coincident(g5,g0)
    c: Distance(g4,g0) = 3
    c: Distance(g1,g3) = 3
    c: Distance(g-5,g1) = 1.5
    c: Distance(g-4,g0) = 47
FEATURE [PartDesign::Pad] Pad004
  BaseFeature = -> Pocket012
  Direction = (0,-1,2e-16)
  Length = 1
  Length2 = 10
  Placement = pos=(0,0,0) rot=(1,0,0;1.5708rad)
  Profile = -> Sketch019
  ReferenceAxis = -> Sketch019 [N_Axis]
  Refine = true
  Suppressed = false
  Type = 0
FEATURE [PartDesign::Pocket] Pocket013
  BaseFeature = -> Pad004
  Direction = (0,1,-2e-16)
  Length = 3
  Length2 = 5
  Placement = pos=(0,0,0) rot=(1,0,0;1.5708rad)
  Profile = -> Sketch018
  ReferenceAxis = -> Sketch018 [N_Axis]
  Refine = true
  Suppressed = false
  Type = 0
FEATURE [Sketcher::SketchObject] Sketch020
  ArcFitTolerance = 1e-06
  AttachmentSupport = -> [Pocket013]
  ExternalGeometry = -> [Pocket013]
  FullyConstrained = true
  MakeInternals = false
  MapMode = 5
  Placement = pos=(0,-3,0) rot=(1,0,0;1.5708rad)
  sketch-geometry (16):
    g0: LineSegment StartX=-56 StartY=67 StartZ=0 EndX=-56 EndY=59 EndZ=0
    g1: LineSegment StartX=-56 StartY=59 StartZ=0 EndX=-46 EndY=59 EndZ=0
    g2: LineSegment StartX=-46 StartY=59 StartZ=0 EndX=-46 EndY=67 EndZ=0
    g3: LineSegment StartX=-46 StartY=67 StartZ=0 EndX=-56 EndY=67 EndZ=0
    g4: LineSegment StartX=-2 StartY=59 StartZ=0 EndX=6 EndY=59 EndZ=0
    g5: LineSegment StartX=6 StartY=59 StartZ=0 EndX=6 EndY=67 EndZ=0
    g6: LineSegment StartX=6 StartY=67 StartZ=0 EndX=-2 EndY=67 EndZ=0
    g7: LineSegment StartX=9 StartY=67 StartZ=0 EndX=17 EndY=67 EndZ=0
    g8: LineSegment StartX=17 StartY=67 StartZ=0 EndX=17 EndY=59 EndZ=0
    g9: LineSegment StartX=17 StartY=59 StartZ=0 EndX=9 EndY=59 EndZ=0
    g10: LineSegment StartX=9 StartY=59 StartZ=0 EndX=9 EndY=67 EndZ=0
    g11: LineSegment StartX=49 StartY=39 StartZ=0 EndX=49 EndY=27 EndZ=0
    g12: LineSegment StartX=49 StartY=27 StartZ=0 EndX=56 EndY=27 EndZ=0
    g13: LineSegment StartX=56 StartY=27 StartZ=0 EndX=56 EndY=39 EndZ=0
    g14: LineSegment StartX=56 StartY=39 StartZ=0 EndX=49 EndY=39 EndZ=0
    g15: LineSegment StartX=-2 StartY=67 StartZ=0 EndX=-2 EndY=59 EndZ=0
  constraints (44):
    c: PointOnObject(g0,g-4)
    c: Coincident(g0,g1)
    c: Horizontal(g1)
    c: Coincident(g1,g2)
    c: PointOnObject(g2,g-3)
    c: Vertical(g2)
    c: Coincident(g2,g3)
    c: Coincident(g3,g0)
    c: PointOnObject(g4,g-5)
    c: Horizontal(g4)
    c: Coincident(g4,g5)
    c: Coincident(g5,g-5)
    c: Coincident(g5,g6)
    c: Horizontal(g6)
    c: Coincident(g-6,g7)
    c: PointOnObject(g7,g-3)
    c: Coincident(g7,g8)
    c: Vertical(g8)
    c: Coincident(g8,g9)
    c: PointOnObject(g9,g-6)
    c: Horizontal(g9)
    c: Coincident(g9,g10)
    c: Coincident(g10,g7)
    c: PointOnObject(g11,g-8)
    c: Vertical(g11)
    c: Coincident(g11,g12)
    c: PointOnObject(g12,g-7)
    c: Horizontal(g12)
    c: Coincident(g12,g13)
    c: Coincident(g13,g-8)
    c: Coincident(g13,g14)
    c: Coincident(g14,g11)
    c: Distance(g1,g3) = 8
    c: Distance(g4,g6) = 8
    c: Distance(g9,g7) = 8
    c: Distance(g2,g0) = 10
    c: Distance(g8,g10) = 8
    c: Distance(g13,g11) = 7
    c: Distance(g12,g14) = 12
    c: Coincident(g15,g6)
    c: Coincident(g15,g4)
    c: Vertical(g15)
    c: Distance(g5,g15) = 8
    c: Coincident(g0,g-4)
FEATURE [PartDesign::Pad] Pad005
  BaseFeature = -> Pocket013
  Direction = (0,-1,2e-16)
  Length = 5
  Length2 = 10
  Placement = pos=(0,0,0) rot=(1,0,0;1.5708rad)
  Profile = -> Sketch020
  ReferenceAxis = -> Sketch020 [N_Axis]
  Refine = true
  Suppressed = false
  Type = 0
FEATURE [PartDesign::Fillet] Fillet002
  Base = -> Pad005 [Edge3552,Edge3566,Edge3712,Edge3580]
  BaseFeature = -> Pad005
  Placement = pos=(0,0,0) rot=(1,0,0;1.5708rad)
  Radius = 4
  Refine = true
  SupportTransform = false
  Suppressed = false
  UseAllEdges = false
FEATURE [Sketcher::SketchObject] Sketch021
  ArcFitTolerance = 1e-06
  AttachmentSupport = -> [Fillet002]
  ExternalGeometry = -> [Fillet002]
  FullyConstrained = true
  MakeInternals = false
  MapMode = 5
  Placement = pos=(0,-8,1.9e-15) rot=(1,0,0;1.5708rad)
  sketch-geometry (4):
    g0: Circle CenterX=-50 CenterY=63 CenterZ=0 NormalX=0 NormalY=0 NormalZ=1 AngleXU=0 Radius=1.25
    g1: Circle CenterX=2 CenterY=63 CenterZ=0 NormalX=0 NormalY=0 NormalZ=1 AngleXU=0 Radius=1.25
    g2: Circle CenterX=13 CenterY=63 CenterZ=0 NormalX=0 NormalY=0 NormalZ=1 AngleXU=0 Radius=1.25
    g3: Circle CenterX=53 CenterY=31 CenterZ=0 NormalX=0 NormalY=0 NormalZ=1 AngleXU=0 Radius=1.25
  constraints (8):
    c: Coincident(g0,g-3)
    c: Coincident(g1,g-4)
    c: Coincident(g2,g-5)
    c: Coincident(g3,g-6)
    c: Diameter(g3) = 2.5
    c: Diameter(g2) = 2.5
    c: Diameter(g1) = 2.5
    c: Diameter(g0) = 2.5
FEATURE [PartDesign::Pocket] Pocket014
  BaseFeature = -> Fillet002
  Direction = (0,1,-2e-16)
  Length = 5
  Length2 = 5
  Placement = pos=(0,0,0) rot=(1,0,0;1.5708rad)
  Profile = -> Sketch021
  ReferenceAxis = -> Sketch021 [N_Axis]
  Refine = true
  Suppressed = false
  Type = 0
FEATURE [Sketcher::SketchObject] Sketch022
  ArcFitTolerance = 1e-06
  AttachmentSupport = -> [Pocket014]
  ExternalGeometry = -> [Pocket014]
  FullyConstrained = true
  MakeInternals = false
  MapMode = 5
  Placement = pos=(0,2.45e-14,70) rot=(0,0,1;3.14159rad)
  sketch-geometry (10):
    g0: LineSegment StartX=-61.75 StartY=20.125 StartZ=0 EndX=-53 EndY=40.25 EndZ=0
    g1: LineSegment StartX=-53 StartY=40.25 StartZ=0 EndX=-25.5 EndY=40.25 EndZ=0
    g2: LineSegment StartX=-25.5 StartY=40.25 StartZ=0 EndX=-16.75 EndY=20.125 EndZ=0
    g3: LineSegment StartX=-16.75 StartY=20.125 StartZ=0 EndX=-25.5 EndY=0 EndZ=0
    g4: LineSegment StartX=-25.5 StartY=0 StartZ=0 EndX=-53 EndY=0 EndZ=0
    g5: LineSegment StartX=-53 StartY=0 StartZ=0 EndX=-61.75 EndY=20.125 EndZ=0
    g6: LineSegment [constr] StartX=-61.75 StartY=20.125 StartZ=0 EndX=-16.75 EndY=20.125 EndZ=0
    g7: LineSegment [constr] StartX=-39.25 StartY=40.25 StartZ=0 EndX=-39.25 EndY=0 EndZ=0
    g8: GeomPoint [constr] X=-39.25 Y=20.125 Z=0
    g9: GeomPoint [constr] X=-39.25 Y=20.125 Z=0
  constraints (23):
    c: Coincident(g0,g1)
    c: Horizontal(g1)
    c: Coincident(g1,g2)
    c: Coincident(g2,g3)
    c: Coincident(g3,g4)
    c: Horizontal(g4)
    c: Coincident(g4,g5)
    c: Coincident(g5,g0)
    c: Coincident(g6,g0)
    c: Coincident(g6,g2)
    c: Horizontal(g6)
    c: Symmetric(g1,g1,g7)
    c: Symmetric(g4,g4,g7)
    c: Vertical(g7)
    c: DistanceX(g6,g6) = 45
    c: PointOnObject(g7,g-3)
    c: PointOnObject(g7,g-1)
    c: Symmetric(g6,g6,g8)
    c: Symmetric(g7,g7,g9)
    c: Coincident(g8,g9)
    c: DistanceX(g1,g-1) = 25.5
    c: Distance(g1,g1) = 27.5
    c: DistanceX(g4,g4) = 27.5
FEATURE [PartDesign::Pad] Pad006  label="Powerplug pad"
  BaseFeature = -> Pocket014
  Direction = (0,0,1)
  Length = 20
  Length2 = 10
  Placement = pos=(0,0,0) rot=(1,0,0;1.5708rad)
  Profile = -> Sketch022
  ReferenceAxis = -> Sketch022 [N_Axis]
  Refine = true
  Suppressed = false
  Type = 0
FEATURE [PartDesign::Fillet] Fillet003
  Base = -> Pad006 [Edge3677,Edge3683]
  BaseFeature = -> Pad006
  Placement = pos=(0,0,0) rot=(1,0,0;1.5708rad)
  Radius = 4
  Refine = true
  SupportTransform = false
  Suppressed = false
  UseAllEdges = false
FEATURE [PartDesign::Fillet] Fillet004
  Base = -> Fillet003 [Edge1227,Edge1]
  BaseFeature = -> Fillet003
  Placement = pos=(0,0,0) rot=(1,0,0;1.5708rad)
  Radius = 3
  Refine = true
  SupportTransform = false
  Suppressed = false
  UseAllEdges = false
FEATURE [Sketcher::SketchObject] Sketch023
  ArcFitTolerance = 1e-06
  AttachmentSupport = -> [Fillet004]
  ExternalGeometry = -> [Fillet004]
  FullyConstrained = true
  MakeInternals = false
  MapMode = 5
  Placement = pos=(0,0,90) rot=(0,0,1;3.14159rad)
  sketch-geometry (7):
    g0: LineSegment StartX=-53.5 StartY=36.5 StartZ=0 EndX=-25 EndY=36.5 EndZ=0
    g1: LineSegment StartX=-25 StartY=36.5 StartZ=0 EndX=-25 EndY=9 EndZ=0
    g2: LineSegment StartX=-25 StartY=9 StartZ=0 EndX=-31 EndY=3 EndZ=0
    g3: LineSegment StartX=-31 StartY=3 StartZ=0 EndX=-47.5 EndY=3 EndZ=0
    g4: LineSegment StartX=-47.5 StartY=3 StartZ=0 EndX=-53.5 EndY=9 EndZ=0
    g5: LineSegment StartX=-53.5 StartY=9 StartZ=0 EndX=-53.5 EndY=36.5 EndZ=0
    g6: LineSegment [constr] StartX=-39.25 StartY=36.5 StartZ=0 EndX=-39.25 EndY=3 EndZ=0
  constraints (20):
    c: Horizontal(g0)
    c: Coincident(g0,g1)
    c: Vertical(g1)
    c: Coincident(g1,g2)
    c: Coincident(g2,g3)
    c: Horizontal(g3)
    c: Coincident(g3,g4)
    c: Coincident(g4,g5)
    c: Coincident(g5,g0)
    c: Vertical(g5)
    c: Symmetric(g0,g0,g6)
    c: Symmetric(g3,g3,g6)
    c: Vertical(g6)
    c: Distance(g1,g5) = 28.5
    c: Distance(g3,g5) = 6
    c: Distance(g4,g3) = 6
    c: Distance(g3,g0) = 33.5
    c: Distance(g1,g3) = 6
    c: PointOnObject(g6,g-4)
    c: Distance(g5,g-3) = 2.5
FEATURE [PartDesign::Pocket] Pocket015  label="PowerPlug pocket"
  BaseFeature = -> Fillet004
  Direction = (0,0,-1)
  Length = 0
  Length2 = 5
  Placement = pos=(0,0,0) rot=(1,0,0;1.5708rad)
  Profile = -> Sketch023
  ReferenceAxis = -> Sketch023 [N_Axis]
  Refine = true
  Suppressed = false
  Type = 3
  UpToFace = -> Fillet004 [Face43]
FEATURE [PartDesign::Fillet] Fillet005
  Base = -> Pocket015 [Edge1380,Edge1385,Edge1384,Edge1383,Edge1381,Edge1382]
  BaseFeature = -> Pocket015
  Placement = pos=(0,0,0) rot=(1,0,0;1.5708rad)
  Radius = 1
  Refine = true
  SupportTransform = false
  Suppressed = false
  UseAllEdges = false
FEATURE [Sketcher::SketchObject] Sketch024
  ArcFitTolerance = 1e-06
  AttachmentSupport = -> [Fillet005]
  ExternalGeometry = -> [Fillet005]
  FullyConstrained = true
  MakeInternals = false
  MapMode = 5
  Placement = pos=(0,0,90) rot=(0,0,1;3.14159rad)
  sketch-geometry (3):
    g0: Circle CenterX=-57.3883 CenterY=20.125 CenterZ=0 NormalX=0 NormalY=0 NormalZ=1 AngleXU=0 Radius=1.1
    g1: Circle CenterX=-21.1117 CenterY=20.125 CenterZ=0 NormalX=0 NormalY=0 NormalZ=1 AngleXU=0 Radius=1.1
    g2: LineSegment [constr] StartX=-57.3883 StartY=20.125 StartZ=0 EndX=-21.1117 EndY=20.125 EndZ=0
  constraints (6):
    c: Coincident(g2,g0)
    c: Coincident(g2,g1)
    c: Coincident(g-3,g0)
    c: Coincident(g1,g-4)
    c: Diameter(g1) = 2.2
    c: Diameter(g0) = 2.2
FEATURE [PartDesign::Pocket] Pocket016  label="PowerPlug holes"
  BaseFeature = -> Fillet005
  Direction = (0,0,-1)
  Length = 0
  Length2 = 5
  Placement = pos=(0,0,0) rot=(1,0,0;1.5708rad)
  Profile = -> Sketch024
  ReferenceAxis = -> Sketch024 [N_Axis]
  Refine = true
  Suppressed = false
  Type = 3
  UpToFace = -> Fillet005 [Face22]
FEATURE [PartDesign::CoordinateSystem] LCS_1
  AttacherType = Attacher::AttachEngine3D
  AttachmentSupport = -> [Pocket016]
  MapMode = 11
  Placement = pos=(-63.5,-40.25,62.5) rot=(0.57735,0.57735,0.57735;4.18879rad)
FEATURE [PartDesign::Body] Body  label="Stack_Module_PSU001"
  AllowCompound = false
  Group = -> [Sketch,Pad,Sketch001,Pocket,Sketch002,Pocket001,Sketch003,Pocket002,MultiTransform,LinearPattern,LinearPattern001,LinearPattern002,Sketch004,Pad001,Sketch006,Pocket003,Sketch007,Pocket004,Sketch008,Pocket005,Sketch009,Pocket006,Sketch010,Pocket007,Sketch011,Pocket008,Sketch012,Pocket009,Sketch013,Pocket010,Sketch014,Pocket011,Fillet,Sketch015,Pad002,Fillet001,Mirrored,Sketch016,Pad003,Sketch017,+20 more]
  Origin = -> Origin001
  Tip = -> Pocket016
FEATURE [App::Part] Part  label="Stack_Module_PSU"
  Group = -> [Body]
  Origin = -> Origin
